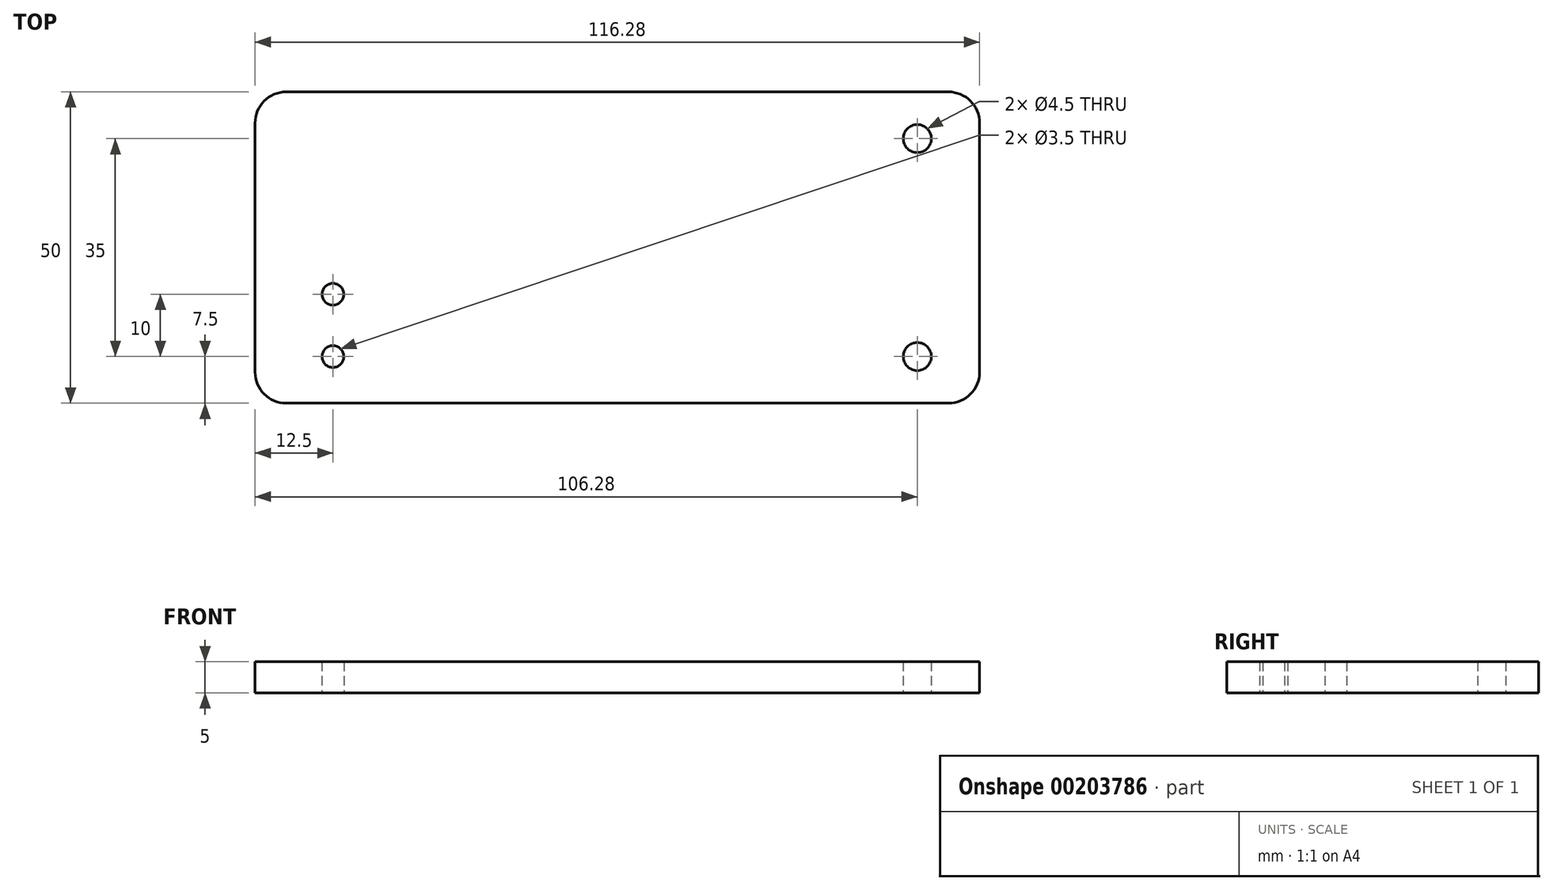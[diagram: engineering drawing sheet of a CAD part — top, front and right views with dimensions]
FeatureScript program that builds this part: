
annotation { "Feature Type Name" : "Feature", "Feature Type Description" : "" }
export const myFeature = defineFeature(function(context is Context, id is Id, definition is map)
    precondition{}
    {
        {
            var Q0;
            Q0=qCreatedBy(makeId("Top.planeOp"),FACE);
            var sketch = newSketch(context, id + "F0", { "sketchPlane" : qUnion([Q0])});
            skLineSegment(sketch, "E0.bottom", {"start": v(58.14, -25) * mm, "end": v(-58.14, -25) * mm});
            skLineSegment(sketch, "E0.top", {"start": v(58.14, 25) * mm, "end": v(-58.14, 25) * mm});
            skLineSegment(sketch, "E0.left", {"start": v(58.14, -25) * mm, "end": v(58.14, 25) * mm});
            skLineSegment(sketch, "E0.right", {"start": v(-58.14, -25) * mm, "end": v(-58.14, 25) * mm});
            skPoint(sketch, "E0.middle", {"position": v(0, 0) * mm});
            skLineSegment(sketch, "E1", {"start": v(58.14, -25) * mm, "end": v(48.14, -25) * mm, "construction": true});
            skLineSegment(sketch, "E2", {"start": v(48.14, -25) * mm, "end": v(48.14, -17.5) * mm, "construction": true});
            skLineSegment(sketch, "E3", {"start": v(48.14, -17.5) * mm, "end": v(48.14, 17.5) * mm, "construction": true});
            skCircle(sketch, "E4", {"center": v(48.14, -17.5) * mm, "radius": 2.25 * mm});
            skCircle(sketch, "E5", {"center": v(48.14, 17.5) * mm, "radius": 2.25 * mm});
            skLineSegment(sketch, "E6", {"start": v(-58.14, -25) * mm, "end": v(-45.64, -25) * mm, "construction": true});
            skLineSegment(sketch, "E7", {"start": v(-45.64, -25) * mm, "end": v(-45.64, -17.5) * mm, "construction": true});
            skLineSegment(sketch, "E8", {"start": v(-45.64, -17.5) * mm, "end": v(-45.64, -7.5) * mm, "construction": true});
            skLineSegment(sketch, "E9", {"start": v(-45.64, -7.5) * mm, "end": v(-45.64, 15.58) * mm, "construction": true});
            skCircle(sketch, "E10", {"center": v(-45.64, -17.5) * mm, "radius": 1.75 * mm});
            skCircle(sketch, "E11", {"center": v(-45.64, -7.5) * mm, "radius": 1.75 * mm});
            skSolve(sketch);
        }
        {
            var Q0;
            Q0=makeQuery(id+"F0.imprint","IMPRINT",FACE,{"disambiguationData":[TD([[makeQuery(id+"F0.imprint","IMPRINT",EDGE,{"derivedFrom":sQuery(id+"F0.wireOp",EDGE,"E0.bottom")}),-1.0]])]});
            extrude(context, id + "F1", {"entities" : qUnion([Q0]), "depth" : 5 * mm, "symmetric" : true});
        }
        {
            var Q0;
            Q0=makeQuery(id+"F1.opExtrude","SWEPT_EDGE",EDGE,{"disambiguationData":[OSD([sQuery(id+"F0.wireOp",EDGE,"E0.bottom"),sQuery(id+"F0.wireOp",EDGE,"E0.right")])]});
            var Q1;
            Q1=makeQuery(id+"F1.opExtrude","SWEPT_EDGE",EDGE,{"disambiguationData":[OSD([sQuery(id+"F0.wireOp",EDGE,"E0.bottom"),sQuery(id+"F0.wireOp",EDGE,"E0.left")])]});
            var Q2;
            Q2=makeQuery(id+"F1.opExtrude","SWEPT_EDGE",EDGE,{"disambiguationData":[OSD([sQuery(id+"F0.wireOp",EDGE,"E0.top"),sQuery(id+"F0.wireOp",EDGE,"E0.left")])]});
            var Q3;
            Q3=makeQuery(id+"F1.opExtrude","SWEPT_EDGE",EDGE,{"disambiguationData":[OSD([sQuery(id+"F0.wireOp",EDGE,"E0.top"),sQuery(id+"F0.wireOp",EDGE,"E0.right")])]});
            fillet(context, id + "F2", {"entities" : qUnion([Q0, Q1, Q2, Q3]), "radius" : 5 * mm, "tangentPropagation" : true, "allowEdgeOverflow" : false});
        }
    });
